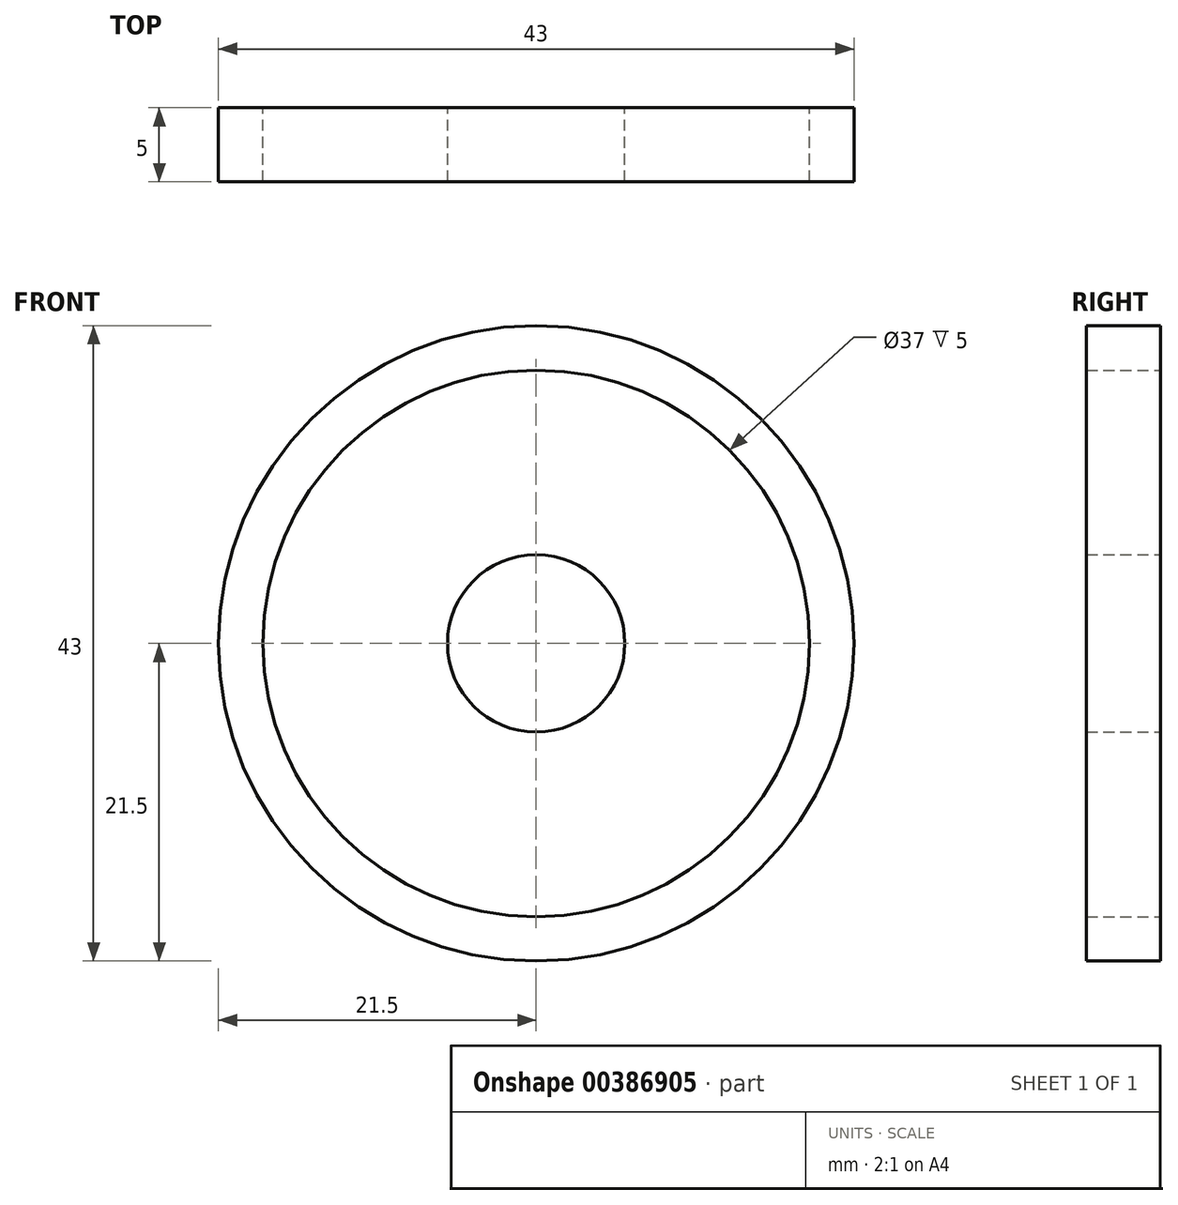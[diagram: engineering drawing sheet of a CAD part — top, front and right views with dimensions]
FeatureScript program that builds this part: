
annotation { "Feature Type Name" : "Feature", "Feature Type Description" : "" }
export const myFeature = defineFeature(function(context is Context, id is Id, definition is map)
    precondition{}
    {
        {
            var Q0;
            Q0=qCreatedBy(makeId("Front.planeOp"),FACE);
            var sketch = newSketch(context, id + "F0", { "sketchPlane" : qUnion([Q0])});
            skLineSegment(sketch, "E0.bottom", {"start": v(21.5, 21.5) * mm, "end": v(-21.5, 21.5) * mm, "construction": true});
            skLineSegment(sketch, "E0.top", {"start": v(21.5, -21.5) * mm, "end": v(-21.5, -21.5) * mm, "construction": true});
            skLineSegment(sketch, "E0.left", {"start": v(21.5, 21.5) * mm, "end": v(21.5, -21.5) * mm, "construction": true});
            skLineSegment(sketch, "E0.right", {"start": v(-21.5, 21.5) * mm, "end": v(-21.5, -21.5) * mm, "construction": true});
            skPoint(sketch, "E0.middle", {"position": v(0, 0) * mm});
            skCircle(sketch, "E1", {"center": v(0, 0) * mm, "radius": 18.5 * mm});
            skCircle(sketch, "E2", {"center": v(0, 0) * mm, "radius": 21.5 * mm});
            skCircle(sketch, "E3", {"center": v(0, 0) * mm, "radius": 2.5 * mm, "construction": true});
            skCircle(sketch, "E4", {"center": v(0, 0) * mm, "radius": 6 * mm});
            skSolve(sketch);
        }
        {
            var Q0;
            Q0 = qSketchRegion(id + "F0", true);
            var Q1;
            Q1=makeQuery(id+"F0.imprint","IMPRINT",FACE,{"disambiguationData":[TD([[makeQuery(id+"F0.imprint","IMPRINT",EDGE,{"derivedFrom":sQuery(id+"F0.wireOp",EDGE,"E4")}),1.0]])]});
            extrude(context, id + "F1", {"entities" : qUnion([Q0, Q1]), "depth" : 5 * mm, "offsetDistance" : 25 * mm});
        }
    });
